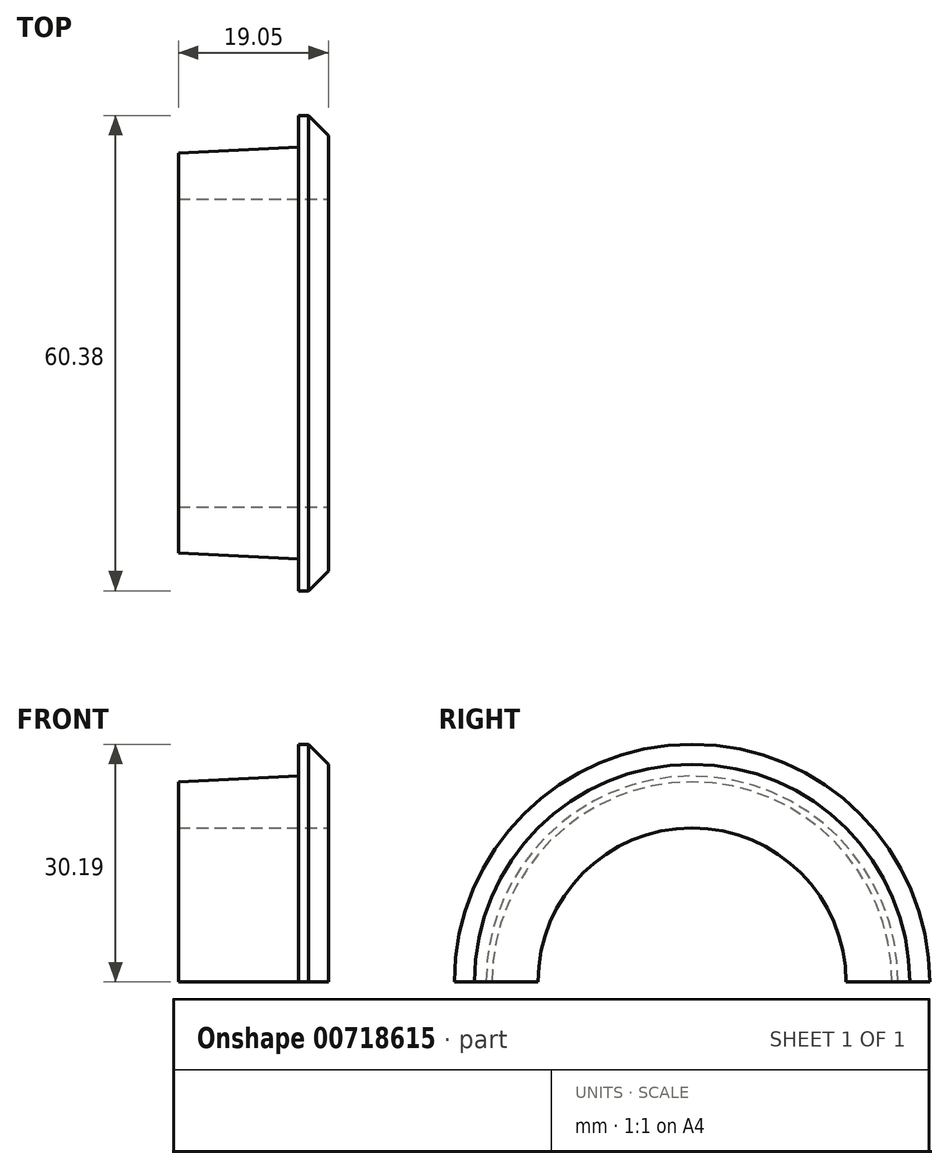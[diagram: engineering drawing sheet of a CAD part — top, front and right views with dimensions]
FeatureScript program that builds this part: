
annotation { "Feature Type Name" : "Feature", "Feature Type Description" : "" }
export const myFeature = defineFeature(function(context is Context, id is Id, definition is map)
    precondition{}
    {
        {
            var Q0;
            Q0=qCreatedBy(makeId("Front.planeOp"),FACE);
            var sketch = newSketch(context, id + "F0", { "sketchPlane" : qUnion([Q0])});
            skLineSegment(sketch, "E0", {"start": v(-12.3, 25.4) * mm, "end": v(-12.3, 19.56) * mm});
            skLineSegment(sketch, "E1", {"start": v(-12.3, 19.56) * mm, "end": v(6.75, 19.56) * mm});
            skLineSegment(sketch, "E2", {"start": v(6.75, 19.56) * mm, "end": v(6.75, 30.19) * mm});
            skLineSegment(sketch, "E3", {"start": v(6.75, 30.19) * mm, "end": v(2.94, 30.19) * mm});
            skLineSegment(sketch, "E4", {"start": v(2.94, 30.19) * mm, "end": v(2.94, 26.16) * mm});
            skLineSegment(sketch, "E5", {"start": v(2.94, 26.16) * mm, "end": v(-12.3, 25.4) * mm});
            skSolve(sketch);
        }
        {
            var Q0;
            Q0=qCreatedBy(makeId("Front.planeOp"),FACE);
            var sketch = newSketch(context, id + "F1", { "sketchPlane" : qUnion([Q0])});
            skLineSegment(sketch, "E6", {"start": v(0, 0) * mm, "end": v(-49.28, 0) * mm});
            skSolve(sketch);
        }
        {
            var Q0;
            Q0=makeQuery(id+"F0.imprint","IMPRINT",FACE,{"disambiguationData":[TD([[makeQuery(id+"F0.imprint","IMPRINT",EDGE,{"derivedFrom":sQuery(id+"F0.wireOp",EDGE,"E0")}),1.0]])]});
            var Q1;
            Q1=sQuery(id+"F1.wireOp",EDGE,"E6");
            revolve(context, id + "F2", {"surfaceOperationType" : NewSurfaceOperationType.NEW, "entities" : qUnion([Q0]), "axis" : qUnion([Q1]), "revolveType" : RevolveType.SYMMETRIC, "angle" : 180 * degree});
        }
        {
            var Q0;
            Q0=makeQuery(id+"F2.opRevolve","SWEPT_EDGE",EDGE,{"disambiguationData":[OSD([sQuery(id+"F0.wireOp",EDGE,"E2"),sQuery(id+"F0.wireOp",EDGE,"E3")])]});
            chamfer(context, id + "F3", {"entities" : qUnion([Q0]), "width" : 2.54 * mm, "tangentPropagation" : true});
        }
    });
